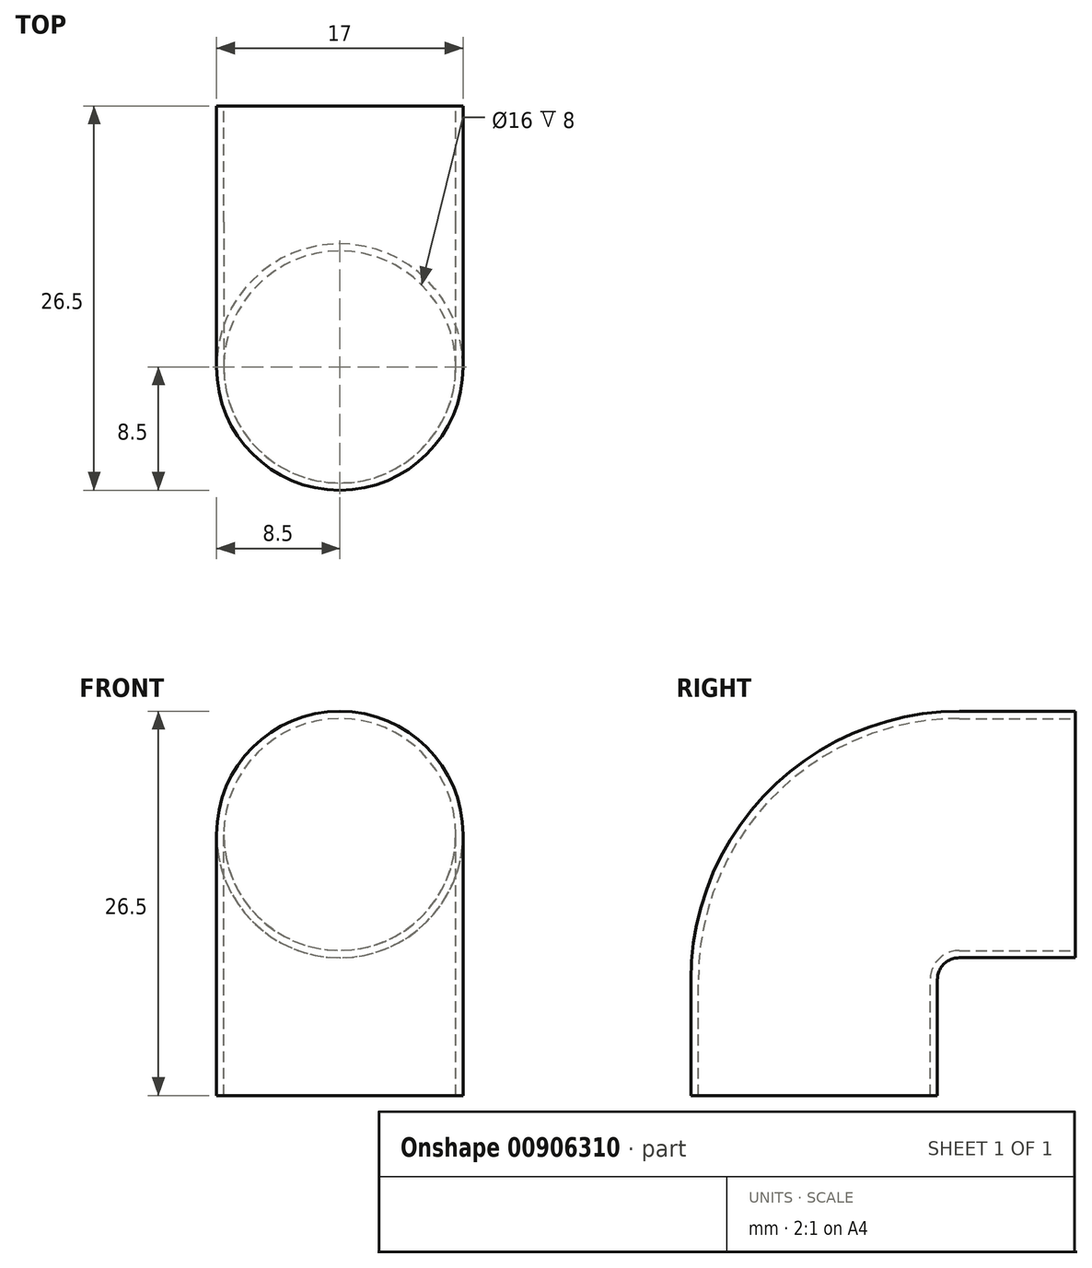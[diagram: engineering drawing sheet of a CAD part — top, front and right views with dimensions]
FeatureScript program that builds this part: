
annotation { "Feature Type Name" : "Feature", "Feature Type Description" : "" }
export const myFeature = defineFeature(function(context is Context, id is Id, definition is map)
    precondition{}
    {
        {
            var Q0;
            Q0=qCreatedBy(makeId("Top.planeOp"),FACE);
            var sketch = newSketch(context, id + "F0", { "sketchPlane" : qUnion([Q0])});
            skCircle(sketch, "E0", {"center": v(0, 0) * mm, "radius": 8.5 * mm});
            skCircle(sketch, "E1", {"center": v(0, 0) * mm, "radius": 8 * mm});
            skSolve(sketch);
        }
        {
            var Q0;
            Q0=qCreatedBy(makeId("Right.planeOp"),FACE);
            var sketch = newSketch(context, id + "F1", { "sketchPlane" : qUnion([Q0])});
            skLineSegment(sketch, "E2", {"start": v(0, 0) * mm, "end": v(0, 8) * mm});
            skLineSegment(sketch, "E3", {"start": v(10, 18) * mm, "end": v(18, 18) * mm});
            skPoint(sketch, "E4.visualSharp", {"position": v(0, 18) * mm});
            skArc(sketch, "E4.filletArc", {"start": v(10, 18) * mm, "mid": v(2.93, 15.07) * mm, "end": v(0, 8) * mm});
            skSolve(sketch);
        }
        {
            var Q0;
            Q0=makeQuery(id+"F0.imprint","IMPRINT",FACE,{"disambiguationData":[TD([[makeQuery(id+"F0.imprint","IMPRINT",EDGE,{"derivedFrom":sQuery(id+"F0.wireOp",EDGE,"E0")}),1.0]])]});
            var Q1;
            Q1=sQuery(id+"F1.wireOp",EDGE,"E2");
            var Q2;
            Q2=sQuery(id+"F1.wireOp",EDGE,"E4.filletArc");
            var Q3;
            Q3=sQuery(id+"F1.wireOp",EDGE,"E3");
            sweep(context, id + "F2", {"profiles" : qUnion([Q0]), "path" : qUnion([Q1, Q2, Q3])});
        }
    });
